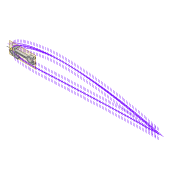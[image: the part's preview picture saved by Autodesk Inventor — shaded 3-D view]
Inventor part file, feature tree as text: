
AUTODESK INVENTOR PART (.ipt)
format: ipt  version: 2022 (Build 260153000, 153)  size: 419,328 bytes
history: native  units: mm
features: extrude x6, sketch x6, projected_geometry x3, plane x2, fillet x2, shell x1
ambient origin geometry x8: Origin, YZ Plane, XZ Plane, XY Plane, X Axis, Y Axis, Z Axis, Center Point
bodies: Solid1 (feature_tree)
feature tree (20):
  extrude  "Extrusion1"  Depth=3.0mm
  shell  "Shell1"  Thickness=6.454mm
  plane  "Work Plane3"
  extrude  "Extrusion10"  Depth=12.0mm
  fillet  "Fillet2"  Radius=18.0mm
  fillet  "Fillet3"  Radius=13.0mm
  extrude  "Extrusion16"  Depth=5.0mm
  extrude  "Extrusion17"  Depth=1.5mm
  extrude  "Extrusion11"  Depth=1.0mm
  plane  "Work Plane4"
  extrude  "Extrusion21"  Depth=10.0mm
  sketch  "Sketch3"  dims[d0=8.0mm d1=0.0mm d2=3.0mm d74=6.454mm]
  sketch  "Sketch29"  dims[d75=63.621mm d76=12.0mm d77=18.0mm d78=13.0mm]
  projected_geometry  "Projected Loop14"
  sketch  "Sketch31"  dims[d79=13.0mm d80=5.0mm]
  sketch  "Sketch37"  dims[d81=1.5mm d82=1.5mm]
  projected_geometry  "Projected Loop20"
  sketch  "Sketch38"  dims[d83=8.0mm d84=0.0mm d85=1.0mm]
  projected_geometry  "Projected Loop21"
  sketch  "Sketch42"  dims[d86=2.7mm d87=4.0mm d88=4.0mm d89=20.0mm d90=0.0mm d93=-8.0mm d97=2.0mm d159=15.0mm d160=5.0mm d161=8.0mm d162=0.0mm d163=25.0mm d164=100.0mm d165=0.0mm d180=2.2mm d181=2.2mm d182=10.0mm d183=0.0mm d168=0.5mm d169=0.872665mm d170=0.5mm d171=0.872665mm]
